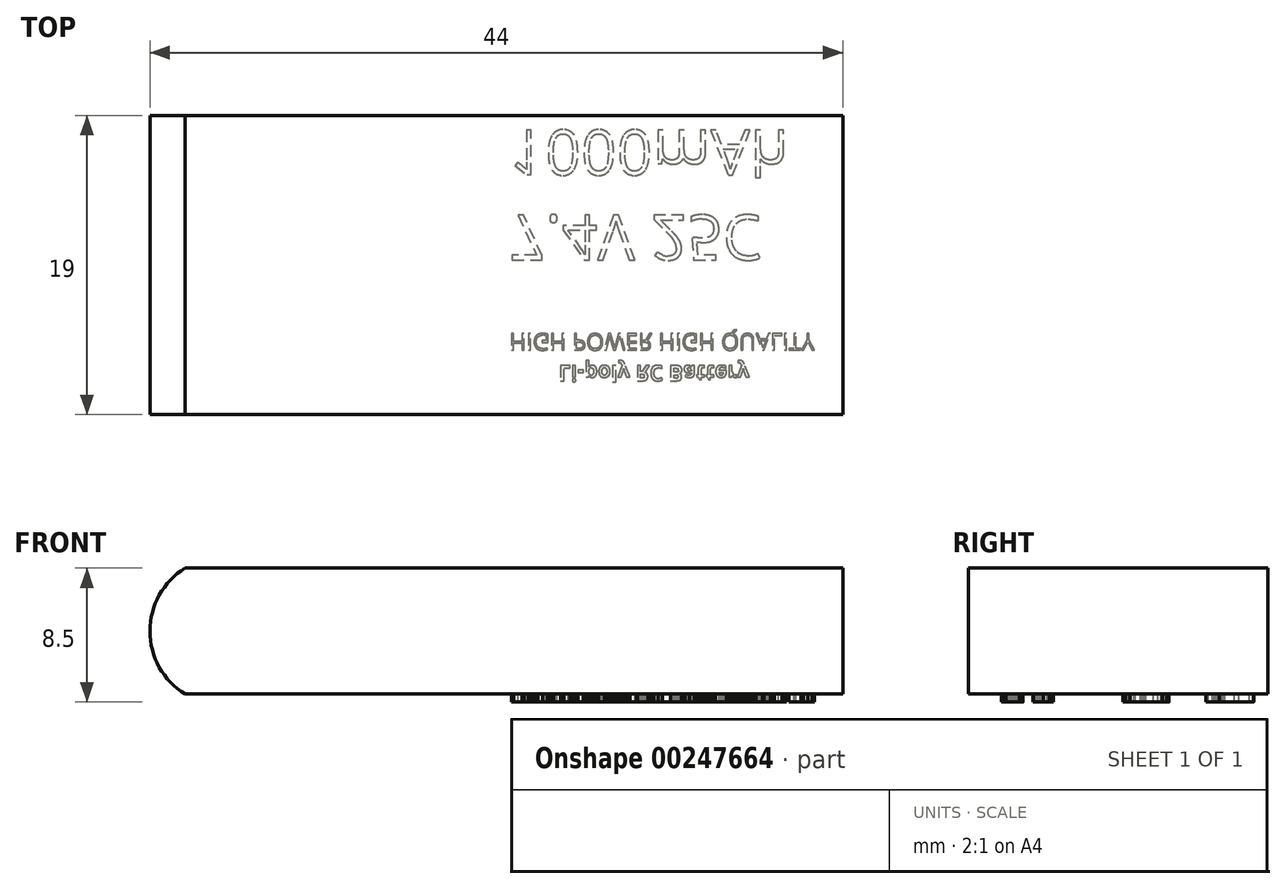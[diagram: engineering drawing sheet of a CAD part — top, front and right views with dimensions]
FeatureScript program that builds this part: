
annotation { "Feature Type Name" : "Feature", "Feature Type Description" : "" }
export const myFeature = defineFeature(function(context is Context, id is Id, definition is map)
    precondition{}
    {
        {
            var Q0;
            Q0=qCreatedBy(makeId("Front.planeOp"),FACE);
            var sketch = newSketch(context, id + "F0", { "sketchPlane" : qUnion([Q0])});
            skLineSegment(sketch, "E0.bottom", {"start": v(22, 4) * mm, "end": v(-22, 4) * mm});
            skLineSegment(sketch, "E0.top", {"start": v(22, -4) * mm, "end": v(-22, -4) * mm});
            skLineSegment(sketch, "E0.left", {"start": v(22, 4) * mm, "end": v(22, -4) * mm});
            skLineSegment(sketch, "E0.right", {"start": v(-22, 4) * mm, "end": v(-22, -4) * mm});
            skPoint(sketch, "E0.middle", {"position": v(0, 0) * mm});
            skArc(sketch, "E1", {"start": v(-22, 0) * mm, "mid": v(-21.4, -2.3) * mm, "end": v(-19.76, -4) * mm});
            skArc(sketch, "E2", {"start": v(-22, 0) * mm, "mid": v(-21.4, 2.3) * mm, "end": v(-19.76, 4) * mm});
            skSolve(sketch);
        }
        {
            var Q0;
            {var subQ1=sQuery(id+"F0.wireOp",EDGE,"E0.left");Q0=makeQuery(id+"F0.imprint","IMPRINT",FACE,{"disambiguationData":[TD([[makeQuery(id+"F0.imprint","IMPRINT",EDGE,{"derivedFrom":subQ1}),-1.0]])]});}
            extrude(context, id + "F1", {"entities" : qUnion([Q0]), "depth" : 19 * mm, "symmetric" : true});
        }
        {
            var Q0;
            Q0=makeQuery(id+"F1.opExtrude","SWEPT_FACE",FACE,{"disambiguationData":[OSD([sQuery(id+"F0.wireOp",EDGE,"E0.top")])]});
            var sketch = newSketch(context, id + "F2", { "sketchPlane" : qUnion([Q0])});
            skText(sketch, "E3", { "text": "Li-poly RC Battery", "fontName": "OpenSans-Bold.ttf"});
            skText(sketch, "E4", { "text": "HIGH POWER HIGH QUALITY", "fontName": "OpenSans-Regular.ttf"});
            skText(sketch, "E5", { "text": "7.4V 25C\n1000mAh", "fontName": "OpenSans-Regular.ttf"});
            const initialGuessF2  = {"E3": [0.00396, 0.00638, 1, 0, 0.00098], "E4": [0.00083, 0.00436, 1, 0, 0.00105], "E5": [0.00083, -0.00317, 1, 0, 0.00286]};
            skSetInitialGuess(sketch, initialGuessF2);
            skSolve(sketch);
        }
        {
            var Q0;
            Q0 = qSketchRegion(id + "F2", true);
            extrude(context, id + "F3", {"entities" : qUnion([Q0]), "operationType" : NewBodyOperationType.ADD, "depth" : .5 * mm});
        }
    });
